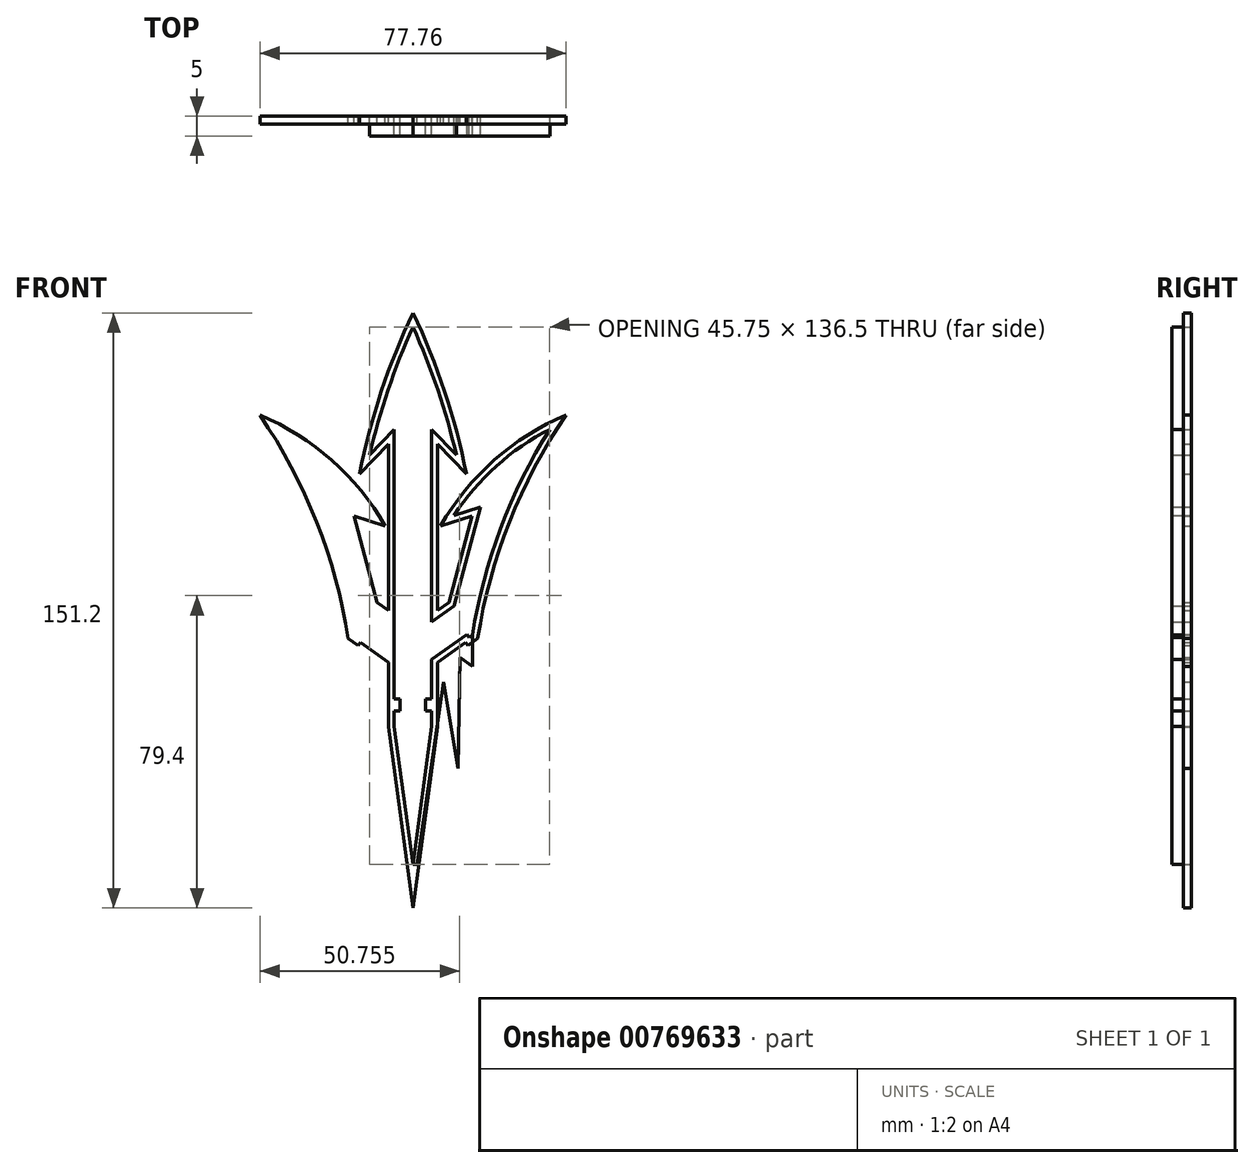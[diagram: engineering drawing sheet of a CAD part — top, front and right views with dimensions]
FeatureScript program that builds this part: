
annotation { "Feature Type Name" : "Feature", "Feature Type Description" : "" }
export const myFeature = defineFeature(function(context is Context, id is Id, definition is map)
    precondition{}
    {
        {
            var Q0;
            Q0=qCreatedBy(makeId("Front.planeOp"),FACE);
            var sketch = newSketch(context, id + "F0", { "sketchPlane" : qUnion([Q0])});
            skLineSegment(sketch, "E0.bottom", {"start": v(4.75, -31.75) * mm, "end": v(-4.75, -31.75) * mm});
            skLineSegment(sketch, "E0.top", {"start": v(4.75, 31.75) * mm, "end": v(-4.75, 31.75) * mm});
            skLineSegment(sketch, "E0.left", {"start": v(4.75, -31.75) * mm, "end": v(4.75, 31.75) * mm});
            skLineSegment(sketch, "E0.right", {"start": v(-4.75, -31.75) * mm, "end": v(-4.75, 31.75) * mm});
            skPoint(sketch, "E0.middle", {"position": v(0, 0) * mm});
            skLineSegment(sketch, "E1", {"start": v(0, 31.75) * mm, "end": v(0, 57.75) * mm});
            skLineSegment(sketch, "E2", {"start": v(0, 31.75) * mm, "end": v(0, 25.25) * mm});
            skLineSegment(sketch, "E3", {"start": v(0, 25.25) * mm, "end": v(11, 25.25) * mm});
            skLineSegment(sketch, "E4", {"start": v(0, 25.25) * mm, "end": v(-11, 25.25) * mm});
            skLineSegment(sketch, "E5", {"start": v(-11, 25.25) * mm, "end": v(0, 57.75) * mm});
            skLineSegment(sketch, "E6", {"start": v(0, 57.75) * mm, "end": v(11, 25.25) * mm});
            skLineSegment(sketch, "E7", {"start": v(-11, 25.25) * mm, "end": v(-4.75, 31.75) * mm});
            skLineSegment(sketch, "E8", {"start": v(4.75, 31.75) * mm, "end": v(11, 25.25) * mm});
            skLineSegment(sketch, "E9.bottom", {"start": v(-4.75, -31.75) * mm, "end": v(4.75, -31.75) * mm});
            skLineSegment(sketch, "E9.top", {"start": v(-4.75, -32.75) * mm, "end": v(4.75, -32.75) * mm});
            skLineSegment(sketch, "E9.left", {"start": v(-4.75, -31.75) * mm, "end": v(-4.75, -32.75) * mm});
            skLineSegment(sketch, "E9.right", {"start": v(4.75, -31.75) * mm, "end": v(4.75, -32.75) * mm});
            skLineSegment(sketch, "E10.top", {"start": v(-4.75, -35.75) * mm, "end": v(4.75, -35.75) * mm});
            skLineSegment(sketch, "E10.left", {"start": v(-4.75, -32.75) * mm, "end": v(-4.75, -35.75) * mm});
            skLineSegment(sketch, "E10.right", {"start": v(4.75, -32.75) * mm, "end": v(4.75, -35.75) * mm});
            skLineSegment(sketch, "E11.top", {"start": v(-4.75, -36.75) * mm, "end": v(4.75, -36.75) * mm});
            skLineSegment(sketch, "E11.left", {"start": v(-4.75, -35.75) * mm, "end": v(-4.75, -36.75) * mm});
            skLineSegment(sketch, "E11.right", {"start": v(4.75, -35.75) * mm, "end": v(4.75, -36.75) * mm});
            skLineSegment(sketch, "E12", {"start": v(-4.75, -36.75) * mm, "end": v(-3.25, -36.75) * mm});
            skLineSegment(sketch, "E13", {"start": v(4.75, -36.75) * mm, "end": v(3.25, -36.75) * mm});
            skLineSegment(sketch, "E14.bottom", {"start": v(-3.25, -36.75) * mm, "end": v(3.25, -36.75) * mm});
            skLineSegment(sketch, "E14.top", {"start": v(-3.25, -39.75) * mm, "end": v(3.25, -39.75) * mm});
            skLineSegment(sketch, "E14.left", {"start": v(-3.25, -36.75) * mm, "end": v(-3.25, -39.75) * mm});
            skLineSegment(sketch, "E14.right", {"start": v(3.25, -36.75) * mm, "end": v(3.25, -39.75) * mm});
            skLineSegment(sketch, "E15.bottom", {"start": v(-4.75, -39.75) * mm, "end": v(4.75, -39.75) * mm});
            skLineSegment(sketch, "E15.top", {"start": v(-4.75, -40.75) * mm, "end": v(4.75, -40.75) * mm});
            skLineSegment(sketch, "E15.left", {"start": v(-4.75, -39.75) * mm, "end": v(-4.75, -40.75) * mm});
            skLineSegment(sketch, "E15.right", {"start": v(4.75, -39.75) * mm, "end": v(4.75, -40.75) * mm});
            skLineSegment(sketch, "E16.top", {"start": v(-4.75, -43.75) * mm, "end": v(4.75, -43.75) * mm});
            skLineSegment(sketch, "E16.left", {"start": v(-4.75, -40.75) * mm, "end": v(-4.75, -43.75) * mm});
            skLineSegment(sketch, "E16.right", {"start": v(4.75, -40.75) * mm, "end": v(4.75, -43.75) * mm});
            skLineSegment(sketch, "E17", {"start": v(0, -43.75) * mm, "end": v(0, -78.75) * mm});
            skLineSegment(sketch, "E18", {"start": v(-4.75, -43.75) * mm, "end": v(0, -78.75) * mm});
            skLineSegment(sketch, "E19", {"start": v(0, -78.75) * mm, "end": v(4.75, -43.75) * mm});
            skLineSegment(sketch, "E20", {"start": v(4.75, -31.75) * mm, "end": v(4.75, -26.75) * mm});
            skLineSegment(sketch, "E21", {"start": v(4.75, 31.75) * mm, "end": v(34.75, 31.75) * mm});
            skLineSegment(sketch, "E22", {"start": v(4.75, -26.75) * mm, "end": v(13.68, -20.33) * mm});
            skLineSegment(sketch, "E23", {"start": v(4.75, -31.75) * mm, "end": v(13.68, -20.33) * mm});
            skLineSegment(sketch, "E24", {"start": v(4.75, -26.75) * mm, "end": v(4.75, -17.25) * mm});
            skLineSegment(sketch, "E25", {"start": v(4.75, -17.25) * mm, "end": v(10.43, -13.16) * mm});
            skLineSegment(sketch, "E26", {"start": v(13.68, -20.33) * mm, "end": v(14.26, -21.14) * mm});
            skLineSegment(sketch, "E27", {"start": v(14.26, -21.14) * mm, "end": v(15.07, -20.55) * mm});
            skArc(sketch, "E28", {"start": v(34.75, 31.75) * mm, "mid": v(22.28, 6.6) * mm, "end": v(15.07, -20.55) * mm});
            skLineSegment(sketch, "E29", {"start": v(10.43, -13.16) * mm, "end": v(10.43, 9.84) * mm});
            skArc(sketch, "E30", {"start": v(34.75, 31.75) * mm, "mid": v(21.17, 22.38) * mm, "end": v(10.43, 9.84) * mm});
            skLineSegment(sketch, "E31", {"start": v(10.43, 9.84) * mm, "end": v(17.1, 11.97) * mm});
            skLineSegment(sketch, "E32", {"start": v(17.1, 11.97) * mm, "end": v(10.43, -13.16) * mm});
            skLineSegment(sketch, "E33", {"start": v(0, -31.75) * mm, "end": v(0, -28.57) * mm});
            skArc(sketch, "E34.MirrorCS", {"start": v(-34.75, 31.75) * mm, "mid": v(-22.28, 6.6) * mm, "end": v(-15.07, -20.55) * mm});
            skLineSegment(sketch, "E35.MirrorCS", {"start": v(-17.1, 11.97) * mm, "end": v(-10.43, -13.16) * mm});
            skArc(sketch, "E36.MirrorCS", {"start": v(-34.75, 31.75) * mm, "mid": v(-21.17, 22.38) * mm, "end": v(-10.43, 9.84) * mm});
            skLineSegment(sketch, "E37.MirrorCS", {"start": v(-10.43, 9.84) * mm, "end": v(-17.1, 11.97) * mm});
            skLineSegment(sketch, "E38.MirrorCS", {"start": v(-4.75, -17.25) * mm, "end": v(-10.43, -13.16) * mm});
            skLineSegment(sketch, "E39.MirrorCS", {"start": v(-4.75, -26.75) * mm, "end": v(-13.68, -20.33) * mm});
            skLineSegment(sketch, "E40.MirrorCS", {"start": v(-14.26, -21.14) * mm, "end": v(-15.07, -20.55) * mm});
            skLineSegment(sketch, "E41.MirrorCS", {"start": v(-13.68, -20.33) * mm, "end": v(-14.26, -21.14) * mm});
            skArc(sketch, "E42", {"start": v(0, 57.75) * mm, "mid": v(-6.31, 41.78) * mm, "end": v(-11, 25.25) * mm});
            skArc(sketch, "E43", {"start": v(11, 25.25) * mm, "mid": v(6.31, 41.78) * mm, "end": v(0, 57.75) * mm});
            skSolve(sketch);
        }
        {
            var Q0;
            {var subQ0=sQuery(id+"F0.wireOp",EDGE,"E1");Q0=makeQuery(id+"F0.imprint","IMPRINT",FACE,{"disambiguationData":[TD([[makeQuery(id+"F0.imprint","IMPRINT",EDGE,{"derivedFrom":subQ0}),1.0]])]});}
            var Q1;
            {var subQ0=sQuery(id+"F0.wireOp",EDGE,"E1");Q1=makeQuery(id+"F0.imprint","IMPRINT",FACE,{"disambiguationData":[TD([[makeQuery(id+"F0.imprint","IMPRINT",EDGE,{"derivedFrom":subQ0}),-1.0]])]});}
            var Q2;
            {var subQ0=sQuery(id+"F0.wireOp",EDGE,"E2");Q2=makeQuery(id+"F0.imprint","IMPRINT",FACE,{"disambiguationData":[TD([[makeQuery(id+"F0.imprint","IMPRINT",EDGE,{"derivedFrom":subQ0}),-1.0]])]});}
            var Q3;
            {var subQ0=sQuery(id+"F0.wireOp",EDGE,"E2");Q3=makeQuery(id+"F0.imprint","IMPRINT",FACE,{"disambiguationData":[TD([[makeQuery(id+"F0.imprint","IMPRINT",EDGE,{"derivedFrom":subQ0}),1.0]])]});}
            var Q4;
            {var subQ6=sQuery(id+"F0.wireOp",EDGE,"E0.bottom");var subQ7=makeQuery(id+"F0.imprint","IMPRINT",VERTEX,{"derivedFrom":subQ6});Q4=makeQuery(id+"F0.imprint","IMPRINT",FACE,{"disambiguationData":[TD([[makeQuery(id+"F0.imprint","IMPRINT",EDGE,{"disambiguationData":[TD([[subQ7,-1.0]])],"derivedFrom":subQ6}),-1.0]])]});}
            var Q5;
            {var subQ0=sQuery(id+"F0.wireOp",EDGE,"E8");Q5=makeQuery(id+"F0.imprint","IMPRINT",FACE,{"disambiguationData":[TD([[makeQuery(id+"F0.imprint","IMPRINT",EDGE,{"derivedFrom":subQ0}),1.0]])]});}
            var Q6;
            {var subQ1=sQuery(id+"F0.wireOp",EDGE,"E22");Q6=makeQuery(id+"F0.imprint","IMPRINT",FACE,{"disambiguationData":[TD([[makeQuery(id+"F0.imprint","IMPRINT",EDGE,{"derivedFrom":subQ1}),1.0]])]});}
            var Q7;
            Q7=makeQuery(id+"F0.imprint","IMPRINT",FACE,{"disambiguationData":[TD([[makeQuery(id+"F0.imprint","IMPRINT",EDGE,{"derivedFrom":sQuery(id+"F0.wireOp",EDGE,"E34.MirrorCS")}),1.0]])]});
            var Q8;
            Q8=makeQuery(id+"F0.imprint","IMPRINT",FACE,{"disambiguationData":[TD([[makeQuery(id+"F0.imprint","IMPRINT",EDGE,{"derivedFrom":sQuery(id+"F0.wireOp",EDGE,"E9.top")}),-1.0]])]});
            var Q9;
            Q9=makeQuery(id+"F0.imprint","IMPRINT",FACE,{"disambiguationData":[TD([[makeQuery(id+"F0.imprint","IMPRINT",EDGE,{"derivedFrom":sQuery(id+"F0.wireOp",EDGE,"E14.top")}),1.0]])]});
            var Q10;
            Q10=makeQuery(id+"F0.imprint","IMPRINT",FACE,{"disambiguationData":[TD([[makeQuery(id+"F0.imprint","IMPRINT",EDGE,{"derivedFrom":sQuery(id+"F0.wireOp",EDGE,"E15.top")}),-1.0]])]});
            var Q11;
            {var subQ0=sQuery(id+"F0.wireOp",EDGE,"E17");Q11=makeQuery(id+"F0.imprint","IMPRINT",FACE,{"disambiguationData":[TD([[makeQuery(id+"F0.imprint","IMPRINT",EDGE,{"derivedFrom":subQ0}),-1.0]])]});}
            var Q12;
            {var subQ0=sQuery(id+"F0.wireOp",EDGE,"E17");Q12=makeQuery(id+"F0.imprint","IMPRINT",FACE,{"disambiguationData":[TD([[makeQuery(id+"F0.imprint","IMPRINT",EDGE,{"derivedFrom":subQ0}),1.0]])]});}
            var Q13;
            {var subQ1=sQuery(id+"F0.wireOp",EDGE,"E14.top");Q13=makeQuery(id+"F0.imprint","IMPRINT",FACE,{"disambiguationData":[TD([[makeQuery(id+"F0.imprint","IMPRINT",EDGE,{"derivedFrom":subQ1}),-1.0]])]});}
            var Q14;
            Q14=makeQuery(id+"F0.imprint","IMPRINT",FACE,{"disambiguationData":[TD([[makeQuery(id+"F0.imprint","IMPRINT",EDGE,{"derivedFrom":sQuery(id+"F0.wireOp",EDGE,"E10.top")}),-1.0]])]});
            var Q15;
            Q15=makeQuery(id+"F0.imprint","IMPRINT",FACE,{"disambiguationData":[TD([[makeQuery(id+"F0.imprint","IMPRINT",EDGE,{"derivedFrom":sQuery(id+"F0.wireOp",EDGE,"E9.top")}),1.0]])]});
            var Q16;
            Q16=makeQuery(id+"F0.imprint","IMPRINT",FACE,{"disambiguationData":[TD([[makeQuery(id+"F0.imprint","IMPRINT",EDGE,{"derivedFrom":sQuery(id+"F0.wireOp",EDGE,"E5")}),1.0]])]});
            var Q17;
            {var subQ0=sQuery(id+"F0.wireOp",EDGE,"E43");var subQ3=sQuery(id+"F0.wireOp",EDGE,"E21");var subQ5=makeQuery(id+"F0.imprint","INTERSECT",VERTEX,{"derivedFrom":[subQ3,subQ0]});Q17=makeQuery(id+"F0.imprint","IMPRINT",FACE,{"disambiguationData":[TD([[makeQuery(id+"F0.imprint","IMPRINT",EDGE,{"disambiguationData":[TD([[subQ5,1.0]])],"derivedFrom":subQ3}),1.0]])]});}
            var Q18;
            {var subQ0=sQuery(id+"F0.wireOp",EDGE,"E43");var subQ3=sQuery(id+"F0.wireOp",EDGE,"E21");var subQ5=makeQuery(id+"F0.imprint","INTERSECT",VERTEX,{"derivedFrom":[subQ3,subQ0]});Q18=makeQuery(id+"F0.imprint","IMPRINT",FACE,{"disambiguationData":[TD([[makeQuery(id+"F0.imprint","IMPRINT",EDGE,{"disambiguationData":[TD([[subQ5,1.0]])],"derivedFrom":subQ3}),-1.0]])]});}
            extrude(context, id + "F1", {"entities" : qUnion([Q0, Q1, Q2, Q3, Q4, Q5, Q6, Q7, Q8, Q9, Q10, Q11, Q12, Q13, Q14, Q15, Q16, Q17, Q18]), "depth" : 5 * mm, "offsetDistance" : 25 * mm});
        }
        {
            var Q0;
            Q0=makeQuery(id+"F1.opExtrude","CAP_FACE",FACE,{"disambiguationData":[OSD([sQuery(id+"F0.wireOp",EDGE,"E0.left"),sQuery(id+"F0.wireOp",EDGE,"E0.right"),sQuery(id+"F0.wireOp",EDGE,"E7"),sQuery(id+"F0.wireOp",EDGE,"E8"),sQuery(id+"F0.wireOp",EDGE,"E9.left"),sQuery(id+"F0.wireOp",EDGE,"E9.right"),sQuery(id+"F0.wireOp",EDGE,"E10.left"),sQuery(id+"F0.wireOp",EDGE,"E10.right"),sQuery(id+"F0.wireOp",EDGE,"E11.top"),sQuery(id+"F0.wireOp",EDGE,"E11.left"),sQuery(id+"F0.wireOp",EDGE,"E11.right"),sQuery(id+"F0.wireOp",EDGE,"E14.left"),sQuery(id+"F0.wireOp",EDGE,"E14.right"),sQuery(id+"F0.wireOp",EDGE,"E15.bottom"),sQuery(id+"F0.wireOp",EDGE,"E15.left"),sQuery(id+"F0.wireOp",EDGE,"E15.right"),sQuery(id+"F0.wireOp",EDGE,"E16.left"),sQuery(id+"F0.wireOp",EDGE,"E16.right"),sQuery(id+"F0.wireOp",EDGE,"E18"),sQuery(id+"F0.wireOp",EDGE,"E19"),sQuery(id+"F0.wireOp",EDGE,"E22"),sQuery(id+"F0.wireOp",EDGE,"E25"),sQuery(id+"F0.wireOp",EDGE,"E26"),sQuery(id+"F0.wireOp",EDGE,"E27"),sQuery(id+"F0.wireOp",EDGE,"E28"),sQuery(id+"F0.wireOp",EDGE,"E30"),sQuery(id+"F0.wireOp",EDGE,"E31"),sQuery(id+"F0.wireOp",EDGE,"E32"),sQuery(id+"F0.wireOp",EDGE,"E34.MirrorCS"),sQuery(id+"F0.wireOp",EDGE,"E35.MirrorCS"),sQuery(id+"F0.wireOp",EDGE,"E36.MirrorCS"),sQuery(id+"F0.wireOp",EDGE,"E37.MirrorCS"),sQuery(id+"F0.wireOp",EDGE,"E38.MirrorCS"),sQuery(id+"F0.wireOp",EDGE,"E39.MirrorCS"),sQuery(id+"F0.wireOp",EDGE,"E40.MirrorCS"),sQuery(id+"F0.wireOp",EDGE,"E41.MirrorCS"),sQuery(id+"F0.wireOp",EDGE,"E42"),sQuery(id+"F0.wireOp",EDGE,"E43")])],"isStart":true});
            var sketch = newSketch(context, id + "F2", { "sketchPlane" : qUnion([Q0])});
            skLineSegment(sketch, "E44", {"start": v(15.07, -20.55) * mm, "end": v(15.07, -28.55) * mm});
            skLineSegment(sketch, "E45", {"start": v(15.07, -28.55) * mm, "end": v(12, -26.24) * mm});
            skLineSegment(sketch, "E46", {"start": v(7.74, -32.5) * mm, "end": v(11.42, -54.37) * mm});
            skLineSegment(sketch, "E47", {"start": v(11.42, -54.37) * mm, "end": v(12, -26.24) * mm});
            skLineSegment(sketch, "E48", {"start": v(0, -78.75) * mm, "end": v(1, -78.75) * mm});
            skLineSegment(sketch, "E49", {"start": v(1, -78.75) * mm, "end": v(7.74, -32.5) * mm});
            skLineSegment(sketch, "E50", {"start": v(0, -78.75) * mm, "end": v(0, -57.62) * mm});
            skLineSegment(sketch, "E51.MirrorCS", {"start": v(-1, -78.75) * mm, "end": v(-7.74, -32.5) * mm});
            skLineSegment(sketch, "E52.MirrorCS", {"start": v(0, -78.75) * mm, "end": v(-1, -78.75) * mm});
            skLineSegment(sketch, "E53.MirrorCS", {"start": v(-7.74, -32.5) * mm, "end": v(-11.42, -54.37) * mm});
            skLineSegment(sketch, "E54.MirrorCS", {"start": v(-11.42, -54.37) * mm, "end": v(-12, -26.24) * mm});
            skLineSegment(sketch, "E55.MirrorCS", {"start": v(-15.07, -20.55) * mm, "end": v(-15.07, -28.55) * mm});
            skLineSegment(sketch, "E56.MirrorCS", {"start": v(-15.07, -28.55) * mm, "end": v(-12, -26.24) * mm});
            skSolve(sketch);
        }
        {
            var Q0;
            Q0=makeQuery(id+"F2.imprint","IMPRINT",FACE,{"disambiguationData":[TD([[makeQuery(id+"F2.imprint","IMPRINT",EDGE,{"derivedFrom":sQuery(id+"F2.wireOp",EDGE,"E44")}),-1.0]])]});
            var Q1;
            Q1=makeQuery(id+"F2.imprint","IMPRINT",FACE,{"disambiguationData":[TD([[makeQuery(id+"F2.imprint","IMPRINT",EDGE,{"derivedFrom":sQuery(id+"F2.wireOp",EDGE,"E51.MirrorCS")}),-1.0]])]});
            extrude(context, id + "F3", {"entities" : qUnion([Q0, Q1]), "oppositeDirection" : true, "depth" : 2 * mm, "offsetDistance" : 25 * mm});
        }
        {
            var Q0;
            Q0=makeQuery(id+"F1.opExtrude","CAP_FACE",FACE,{"disambiguationData":[OSD([sQuery(id+"F0.wireOp",EDGE,"E0.left"),sQuery(id+"F0.wireOp",EDGE,"E0.right"),sQuery(id+"F0.wireOp",EDGE,"E7"),sQuery(id+"F0.wireOp",EDGE,"E8"),sQuery(id+"F0.wireOp",EDGE,"E9.left"),sQuery(id+"F0.wireOp",EDGE,"E9.right"),sQuery(id+"F0.wireOp",EDGE,"E10.left"),sQuery(id+"F0.wireOp",EDGE,"E10.right"),sQuery(id+"F0.wireOp",EDGE,"E11.top"),sQuery(id+"F0.wireOp",EDGE,"E11.left"),sQuery(id+"F0.wireOp",EDGE,"E11.right"),sQuery(id+"F0.wireOp",EDGE,"E14.left"),sQuery(id+"F0.wireOp",EDGE,"E14.right"),sQuery(id+"F0.wireOp",EDGE,"E15.bottom"),sQuery(id+"F0.wireOp",EDGE,"E15.left"),sQuery(id+"F0.wireOp",EDGE,"E15.right"),sQuery(id+"F0.wireOp",EDGE,"E16.left"),sQuery(id+"F0.wireOp",EDGE,"E16.right"),sQuery(id+"F0.wireOp",EDGE,"E18"),sQuery(id+"F0.wireOp",EDGE,"E19"),sQuery(id+"F0.wireOp",EDGE,"E22"),sQuery(id+"F0.wireOp",EDGE,"E25"),sQuery(id+"F0.wireOp",EDGE,"E26"),sQuery(id+"F0.wireOp",EDGE,"E27"),sQuery(id+"F0.wireOp",EDGE,"E28"),sQuery(id+"F0.wireOp",EDGE,"E30"),sQuery(id+"F0.wireOp",EDGE,"E31"),sQuery(id+"F0.wireOp",EDGE,"E32"),sQuery(id+"F0.wireOp",EDGE,"E34.MirrorCS"),sQuery(id+"F0.wireOp",EDGE,"E35.MirrorCS"),sQuery(id+"F0.wireOp",EDGE,"E36.MirrorCS"),sQuery(id+"F0.wireOp",EDGE,"E37.MirrorCS"),sQuery(id+"F0.wireOp",EDGE,"E38.MirrorCS"),sQuery(id+"F0.wireOp",EDGE,"E39.MirrorCS"),sQuery(id+"F0.wireOp",EDGE,"E40.MirrorCS"),sQuery(id+"F0.wireOp",EDGE,"E41.MirrorCS"),sQuery(id+"F0.wireOp",EDGE,"E42"),sQuery(id+"F0.wireOp",EDGE,"E43")])],"isStart":true});
            var sketch = newSketch(context, id + "F4", { "sketchPlane" : qUnion([Q0])});
            skLineSegment(sketch, "E57.0", {"start": v(6.25, -14.32) * mm, "end": v(6.25, 28.03) * mm});
            skLineSegment(sketch, "E57.1", {"start": v(9.12, -12.26) * mm, "end": v(6.25, -14.32) * mm});
            skLineSegment(sketch, "E57.2", {"start": v(14.95, 9.7) * mm, "end": v(9.12, -12.26) * mm});
            skLineSegment(sketch, "E57.3", {"start": v(7.06, 7.19) * mm, "end": v(14.95, 9.7) * mm});
            skArc(sketch, "E57.4", {"start": v(38.88, 35.32) * mm, "mid": v(20.62, 23.9) * mm, "end": v(7.06, 7.19) * mm});
            skArc(sketch, "E57.5", {"start": v(16.46, -21.4) * mm, "mid": v(24.5, 8.2) * mm, "end": v(38.88, 35.32) * mm});
            skLineSegment(sketch, "E57.6", {"start": v(13.92, -23.23) * mm, "end": v(16.46, -21.4) * mm});
            skLineSegment(sketch, "E57.7", {"start": v(13.34, -22.42) * mm, "end": v(13.92, -23.23) * mm});
            skLineSegment(sketch, "E57.8", {"start": v(6.25, -27.52) * mm, "end": v(13.34, -22.42) * mm});
            skLineSegment(sketch, "E57.9", {"start": v(6.25, -38.25) * mm, "end": v(6.25, -27.52) * mm});
            skLineSegment(sketch, "E57.10", {"start": v(4.75, -38.25) * mm, "end": v(6.25, -38.25) * mm});
            skLineSegment(sketch, "E57.11", {"start": v(-16.46, -21.4) * mm, "end": v(-13.92, -23.23) * mm});
            skArc(sketch, "E57.12", {"start": v(-38.88, 35.32) * mm, "mid": v(-24.5, 8.2) * mm, "end": v(-16.46, -21.4) * mm});
            skArc(sketch, "E57.13", {"start": v(-7.06, 7.19) * mm, "mid": v(-20.62, 23.9) * mm, "end": v(-38.88, 35.32) * mm});
            skLineSegment(sketch, "E57.14", {"start": v(-14.95, 9.7) * mm, "end": v(-7.06, 7.19) * mm});
            skLineSegment(sketch, "E57.15", {"start": v(-9.12, -12.26) * mm, "end": v(-14.95, 9.7) * mm});
            skLineSegment(sketch, "E57.16", {"start": v(-6.25, -14.32) * mm, "end": v(-9.12, -12.26) * mm});
            skArc(sketch, "E57.17", {"start": v(13.57, 20.41) * mm, "mid": v(8.06, 41.28) * mm, "end": v(0, 61.3) * mm});
            skArc(sketch, "E57.18", {"start": v(0, 61.3) * mm, "mid": v(-8.06, 41.28) * mm, "end": v(-13.57, 20.41) * mm});
            skLineSegment(sketch, "E57.19", {"start": v(-13.57, 20.41) * mm, "end": v(-6.25, 28.03) * mm});
            skLineSegment(sketch, "E57.20", {"start": v(-6.25, 28.03) * mm, "end": v(-6.25, -14.32) * mm});
            skLineSegment(sketch, "E57.21", {"start": v(-13.92, -23.23) * mm, "end": v(-13.34, -22.42) * mm});
            skLineSegment(sketch, "E57.22", {"start": v(-13.34, -22.42) * mm, "end": v(-6.25, -27.52) * mm});
            skLineSegment(sketch, "E57.23", {"start": v(-6.25, -27.52) * mm, "end": v(-6.25, -38.25) * mm});
            skLineSegment(sketch, "E57.24", {"start": v(-6.25, -38.25) * mm, "end": v(-4.75, -38.25) * mm});
            skLineSegment(sketch, "E57.25", {"start": v(-4.75, -38.25) * mm, "end": v(-4.75, -38.25) * mm});
            skLineSegment(sketch, "E57.26", {"start": v(-4.75, -38.25) * mm, "end": v(-6.25, -38.25) * mm});
            skLineSegment(sketch, "E57.27", {"start": v(-6.25, -38.25) * mm, "end": v(-6.25, -43.85) * mm});
            skLineSegment(sketch, "E57.28", {"start": v(-6.25, -43.85) * mm, "end": v(0, -89.9) * mm});
            skLineSegment(sketch, "E57.29", {"start": v(0, -89.9) * mm, "end": v(6.25, -43.85) * mm});
            skLineSegment(sketch, "E57.30", {"start": v(6.25, -43.85) * mm, "end": v(6.25, -38.25) * mm});
            skLineSegment(sketch, "E57.31", {"start": v(6.25, -38.25) * mm, "end": v(4.75, -38.25) * mm});
            skLineSegment(sketch, "E57.32", {"start": v(6.25, 28.03) * mm, "end": v(13.57, 20.41) * mm});
            skLineSegment(sketch, "E57.33", {"start": v(4.75, -38.25) * mm, "end": v(4.75, -38.25) * mm});
            skSolve(sketch);
        }
        {
            var Q0;
            Q0=makeQuery(id+"F4.imprint","IMPRINT",FACE,{"disambiguationData":[TD([[makeQuery(id+"F4.imprint","IMPRINT",EDGE,{"derivedFrom":sQuery(id+"F4.wireOp",EDGE,"E57.0")}),1.0]])]});
            extrude(context, id + "F5", {"entities" : qUnion([Q0]), "oppositeDirection" : true, "depth" : 2 * mm, "offsetDistance" : 25 * mm});
        }
    });
